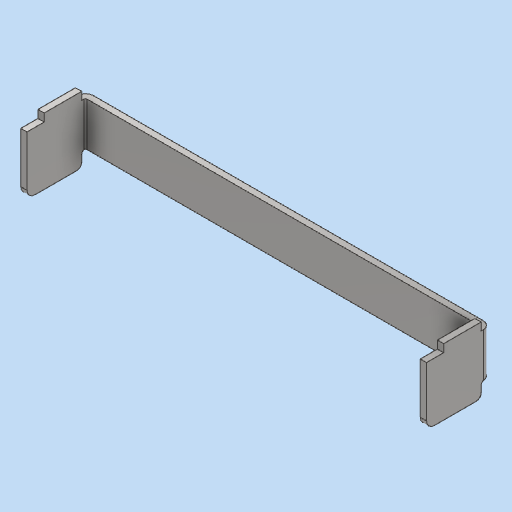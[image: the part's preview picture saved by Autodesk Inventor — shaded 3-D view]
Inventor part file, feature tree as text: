
AUTODESK INVENTOR PART (.ipt)
format: ipt  version: 2023 (Build 270158000, 158)  size: 293,376 bytes
history: native  units: mm
features: other x4, extrude x1
ambient origin geometry x8: Origin, YZ Plane, XZ Plane, XY Plane, X Axis, Y Axis, Z Axis, Center Point
bodies: Body1 (feature_tree)
feature tree (5):
  other  "實體1"
  extrude  "擠出1"  Depth=2.0mm TaperAngle=0.0deg
  other  "折彎零件1"
  other  "折彎零件2"
  other  "定義1"
